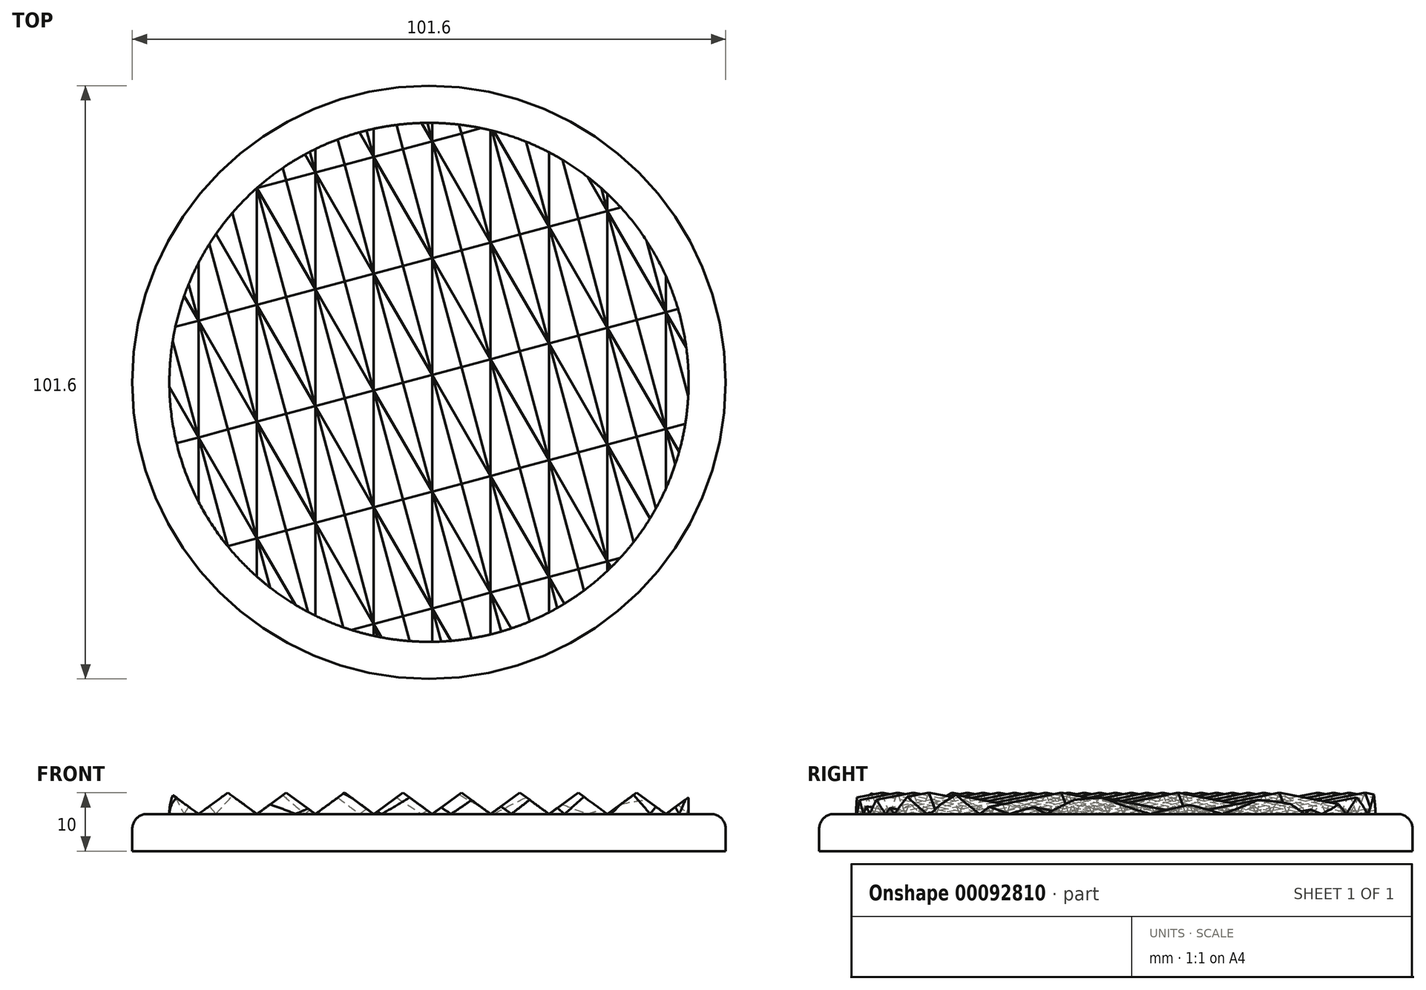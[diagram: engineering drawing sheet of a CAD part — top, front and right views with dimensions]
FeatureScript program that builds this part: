
annotation { "Feature Type Name" : "Feature", "Feature Type Description" : "" }
export const myFeature = defineFeature(function(context is Context, id is Id, definition is map)
    precondition{}
    {
        {
            var Q0;
            Q0=qCreatedBy(makeId("Top.planeOp"),FACE);
            var sketch = newSketch(context, id + "F0", { "sketchPlane" : qUnion([Q0])});
            skCircle(sketch, "E0", {"center": v(0, 0) * mm, "radius": 50.8 * mm});
            skCircle(sketch, "E1.0", {"center": v(0, 0) * mm, "radius": 44.45 * mm});
            skLineSegment(sketch, "E2", {"start": v(0, 110.46) * mm, "end": v(0, -125.45) * mm, "construction": true});
            skLineSegment(sketch, "E3", {"start": v(-101.34, -44.45) * mm, "end": v(105.07, -44.45) * mm, "construction": true});
            skLineSegment(sketch, "E4", {"start": v(129.04, 23.18) * mm, "end": v(-73.12, -93.54) * mm, "construction": true});
            skPoint(sketch, "E5", {"position": v(0, -44.45) * mm});
            skPoint(sketch, "E6", {"position": v(22.23, -38.5) * mm});
            skSolve(sketch);
        }
        {
            var Q0;
            Q0=makeQuery(id+"F0.imprint","IMPRINT",FACE,{"disambiguationData":[TD([[makeQuery(id+"F0.imprint","IMPRINT",EDGE,{"derivedFrom":sQuery(id+"F0.wireOp",EDGE,"E0")}),1.0]])]});
            extrude(context, id + "F1", {"entities" : qUnion([Q0]), "depth" : 6.35 * mm});
        }
        {
            var Q0;
            Q0=makeQuery(id+"F0.imprint","IMPRINT",FACE,{"disambiguationData":[TD([[makeQuery(id+"F0.imprint","IMPRINT",EDGE,{"derivedFrom":sQuery(id+"F0.wireOp",EDGE,"E1.0")}),1.0]])]});
            extrude(context, id + "F2", {"entities" : qUnion([Q0]), "operationType" : NewBodyOperationType.ADD, "depth" : 10 * mm});
        }
        {
            var Q0;
            Q0=makeQuery(id+"F2.opExtrude","CAP_FACE",FACE,{"disambiguationData":[OSD([sQuery(id+"F0.wireOp",EDGE,"E1.0")])],"isStart":false});
            var sketch = newSketch(context, id + "F3", { "sketchPlane" : qUnion([Q0])});
            skPoint(sketch, "E7.0", {"position": v(0, -44.45) * mm});
            skPoint(sketch, "E7.1", {"position": v(22.23, -38.5) * mm});
            skLineSegment(sketch, "E8.0", {"start": v(-101.34, -44.45) * mm, "end": v(105.07, -44.45) * mm, "construction": true});
            skLineSegment(sketch, "E8.1", {"start": v(129.04, 23.18) * mm, "end": v(-73.12, -93.54) * mm, "construction": true});
            skPoint(sketch, "E9", {"position": v(11.91, -44.45) * mm});
            skLineSegment(sketch, "E10", {"start": v(-34.53, 128.88) * mm, "end": v(21.6, -80.6) * mm, "construction": true});
            skSolve(sketch);
        }
        {
            var Q0;
            Q0=sQuery(id+"F3.wireOp",EDGE,"E8.1");
            var Q1;
            Q1=sQuery(id+"F0.wireOp",VERTEX,"E6");
            cPlane(context, id + "F4", {"entities" : qUnion([Q0, Q1]), "cplaneType" : CPlaneType.LINE_ANGLE, "offset" : 152.4 * mm, "angle" : 0 * degree, "width" : 152.4 * mm, "height" : 152.4 * mm});
        }
        {
            var Q0;
            Q0=sQuery(id+"F3.wireOp",EDGE,"E8.0");
            var Q1;
            Q1=sQuery(id+"F0.wireOp",VERTEX,"E5");
            cPlane(context, id + "F5", {"entities" : qUnion([Q0, Q1]), "cplaneType" : CPlaneType.LINE_ANGLE, "offset" : 152.4 * mm, "angle" : 0 * degree, "width" : 152.4 * mm, "height" : 152.4 * mm});
        }
        {
            var Q0;
            Q0=qCreatedBy(id+"F5.planeOp",FACE);
            var sketch = newSketch(context, id + "F6", { "sketchPlane" : qUnion([Q0])});
            skPoint(sketch, "E11.0", {"position": v(0, 0) * mm});
            skLineSegment(sketch, "E12", {"start": v(0, 24.1) * mm, "end": v(0, -15.53) * mm, "construction": true});
            skLineSegment(sketch, "E13.0", {"start": v(-44.45, 10) * mm, "end": v(44.45, 10) * mm, "construction": true});
            skLineSegment(sketch, "E14.0", {"start": v(-50.8, 6.35) * mm, "end": v(50.8, 6.35) * mm, "construction": true});
            skLineSegment(sketch, "E15", {"start": v(44.45, 10) * mm, "end": v(39.45, 6.35) * mm});
            skLineSegment(sketch, "E16", {"start": v(39.45, 6.35) * mm, "end": v(34.45, 10) * mm});
            skLineSegment(sketch, "E17", {"start": v(34.45, 10) * mm, "end": v(44.45, 10) * mm});
            skLineSegment(sketch, "E18.1.0.0", {"start": v(24.45, 10) * mm, "end": v(34.45, 10) * mm});
            skLineSegment(sketch, "E18.1.0.1", {"start": v(29.45, 6.35) * mm, "end": v(24.45, 10) * mm});
            skLineSegment(sketch, "E18.1.0.2", {"start": v(34.45, 10) * mm, "end": v(29.45, 6.35) * mm});
            skLineSegment(sketch, "E18.2.0.0", {"start": v(14.45, 10) * mm, "end": v(24.45, 10) * mm});
            skLineSegment(sketch, "E18.2.0.1", {"start": v(19.45, 6.35) * mm, "end": v(14.45, 10) * mm});
            skLineSegment(sketch, "E18.2.0.2", {"start": v(24.45, 10) * mm, "end": v(19.45, 6.35) * mm});
            skLineSegment(sketch, "E18.3.0.0", {"start": v(4.45, 10) * mm, "end": v(14.45, 10) * mm});
            skLineSegment(sketch, "E18.3.0.1", {"start": v(9.45, 6.35) * mm, "end": v(4.45, 10) * mm});
            skLineSegment(sketch, "E18.3.0.2", {"start": v(14.45, 10) * mm, "end": v(9.45, 6.35) * mm});
            skLineSegment(sketch, "E18.4.0.0", {"start": v(-5.55, 10) * mm, "end": v(4.45, 10) * mm});
            skLineSegment(sketch, "E18.4.0.1", {"start": v(-0.55, 6.35) * mm, "end": v(-5.55, 10) * mm});
            skLineSegment(sketch, "E18.4.0.2", {"start": v(4.45, 10) * mm, "end": v(-0.55, 6.35) * mm});
            skLineSegment(sketch, "E18.5.0.0", {"start": v(-15.55, 10) * mm, "end": v(-5.55, 10) * mm});
            skLineSegment(sketch, "E18.5.0.1", {"start": v(-10.55, 6.35) * mm, "end": v(-15.55, 10) * mm});
            skLineSegment(sketch, "E18.5.0.2", {"start": v(-5.55, 10) * mm, "end": v(-10.55, 6.35) * mm});
            skLineSegment(sketch, "E18.6.0.0", {"start": v(-25.55, 10) * mm, "end": v(-15.55, 10) * mm});
            skLineSegment(sketch, "E18.6.0.1", {"start": v(-20.55, 6.35) * mm, "end": v(-25.55, 10) * mm});
            skLineSegment(sketch, "E18.6.0.2", {"start": v(-15.55, 10) * mm, "end": v(-20.55, 6.35) * mm});
            skLineSegment(sketch, "E18.7.0.0", {"start": v(-35.55, 10) * mm, "end": v(-25.55, 10) * mm});
            skLineSegment(sketch, "E18.7.0.1", {"start": v(-30.55, 6.35) * mm, "end": v(-35.55, 10) * mm});
            skLineSegment(sketch, "E18.7.0.2", {"start": v(-25.55, 10) * mm, "end": v(-30.55, 6.35) * mm});
            skLineSegment(sketch, "E18.8.0.0", {"start": v(-45.55, 10) * mm, "end": v(-35.55, 10) * mm});
            skLineSegment(sketch, "E18.8.0.1", {"start": v(-40.55, 6.35) * mm, "end": v(-45.55, 10) * mm});
            skLineSegment(sketch, "E18.8.0.2", {"start": v(-35.55, 10) * mm, "end": v(-40.55, 6.35) * mm});
            skLineSegment(sketch, "E18.direction1", {"start": v(34.45, 10) * mm, "end": v(24.45, 10) * mm, "construction": true});
            skSolve(sketch);
        }
        {
            var Q0;
            Q0=makeQuery(id+"F6.imprint","IMPRINT",FACE,{"disambiguationData":[TD([[makeQuery(id+"F6.imprint","IMPRINT",EDGE,{"derivedFrom":sQuery(id+"F6.wireOp",EDGE,"E15")}),-1.0]])]});
            var Q1;
            Q1=makeQuery(id+"F6.imprint","IMPRINT",FACE,{"disambiguationData":[TD([[makeQuery(id+"F6.imprint","IMPRINT",EDGE,{"derivedFrom":sQuery(id+"F6.wireOp",EDGE,"E18.1.0.0")}),-1.0]])]});
            var Q2;
            Q2=makeQuery(id+"F6.imprint","IMPRINT",FACE,{"disambiguationData":[TD([[makeQuery(id+"F6.imprint","IMPRINT",EDGE,{"derivedFrom":sQuery(id+"F6.wireOp",EDGE,"E18.2.0.0")}),-1.0]])]});
            var Q3;
            Q3=makeQuery(id+"F6.imprint","IMPRINT",FACE,{"disambiguationData":[TD([[makeQuery(id+"F6.imprint","IMPRINT",EDGE,{"derivedFrom":sQuery(id+"F6.wireOp",EDGE,"E18.3.0.0")}),-1.0]])]});
            var Q4;
            Q4=makeQuery(id+"F6.imprint","IMPRINT",FACE,{"disambiguationData":[TD([[makeQuery(id+"F6.imprint","IMPRINT",EDGE,{"derivedFrom":sQuery(id+"F6.wireOp",EDGE,"E18.4.0.0")}),-1.0]])]});
            var Q5;
            Q5=makeQuery(id+"F6.imprint","IMPRINT",FACE,{"disambiguationData":[TD([[makeQuery(id+"F6.imprint","IMPRINT",EDGE,{"derivedFrom":sQuery(id+"F6.wireOp",EDGE,"E18.5.0.0")}),-1.0]])]});
            var Q6;
            Q6=makeQuery(id+"F6.imprint","IMPRINT",FACE,{"disambiguationData":[TD([[makeQuery(id+"F6.imprint","IMPRINT",EDGE,{"derivedFrom":sQuery(id+"F6.wireOp",EDGE,"E18.6.0.0")}),-1.0]])]});
            var Q7;
            Q7=makeQuery(id+"F6.imprint","IMPRINT",FACE,{"disambiguationData":[TD([[makeQuery(id+"F6.imprint","IMPRINT",EDGE,{"derivedFrom":sQuery(id+"F6.wireOp",EDGE,"E18.7.0.0")}),-1.0]])]});
            var Q8;
            Q8=makeQuery(id+"F6.imprint","IMPRINT",FACE,{"disambiguationData":[TD([[makeQuery(id+"F6.imprint","IMPRINT",EDGE,{"derivedFrom":sQuery(id+"F6.wireOp",EDGE,"E18.8.0.0")}),-1.0]])]});
            extrude(context, id + "F7", {"entities" : qUnion([Q0, Q1, Q2, Q3, Q4, Q5, Q6, Q7, Q8]), "operationType" : NewBodyOperationType.REMOVE, "depth" : 88.9 * mm});
        }
        {
            var Q0;
            Q0=qCreatedBy(id+"F4.planeOp",FACE);
            var sketch = newSketch(context, id + "F8", { "sketchPlane" : qUnion([Q0])});
            skPoint(sketch, "E19.0", {"position": v(0, 0) * mm});
            skLineSegment(sketch, "E20", {"start": v(0, 40.07) * mm, "end": v(0, -5.08) * mm, "construction": true});
            skLineSegment(sketch, "E21.0", {"start": v(-50.8, 6.35) * mm, "end": v(50.8, 6.35) * mm, "construction": true});
            skPoint(sketch, "E22.0", {"position": v(44.13, 10) * mm});
            skPoint(sketch, "E22.1", {"position": v(-43.88, 10) * mm});
            skLineSegment(sketch, "E23", {"start": v(-43.88, 10) * mm, "end": v(44.13, 10) * mm, "construction": true});
            skLineSegment(sketch, "E24", {"start": v(-43.88, 10) * mm, "end": v(-38.88, 6.35) * mm});
            skLineSegment(sketch, "E25", {"start": v(-38.88, 6.35) * mm, "end": v(-33.88, 10) * mm});
            skLineSegment(sketch, "E26", {"start": v(-33.88, 10) * mm, "end": v(-43.88, 10) * mm});
            skLineSegment(sketch, "E27.1.0.0", {"start": v(-28.88, 6.35) * mm, "end": v(-23.88, 10) * mm});
            skLineSegment(sketch, "E27.1.0.1", {"start": v(-23.88, 10) * mm, "end": v(-33.88, 10) * mm});
            skPoint(sketch, "E27.1.0.2", {"position": v(-33.88, 10) * mm});
            skLineSegment(sketch, "E27.1.0.3", {"start": v(-33.88, 10) * mm, "end": v(-28.88, 6.35) * mm});
            skLineSegment(sketch, "E27.2.0.0", {"start": v(-18.88, 6.35) * mm, "end": v(-13.88, 10) * mm});
            skLineSegment(sketch, "E27.2.0.1", {"start": v(-13.88, 10) * mm, "end": v(-23.88, 10) * mm});
            skPoint(sketch, "E27.2.0.2", {"position": v(-23.88, 10) * mm});
            skLineSegment(sketch, "E27.2.0.3", {"start": v(-23.88, 10) * mm, "end": v(-18.88, 6.35) * mm});
            skLineSegment(sketch, "E27.3.0.0", {"start": v(-8.88, 6.35) * mm, "end": v(-3.88, 10) * mm});
            skLineSegment(sketch, "E27.3.0.1", {"start": v(-3.88, 10) * mm, "end": v(-13.88, 10) * mm});
            skPoint(sketch, "E27.3.0.2", {"position": v(-13.88, 10) * mm});
            skLineSegment(sketch, "E27.3.0.3", {"start": v(-13.88, 10) * mm, "end": v(-8.88, 6.35) * mm});
            skLineSegment(sketch, "E27.4.0.0", {"start": v(1.12, 6.35) * mm, "end": v(6.12, 10) * mm});
            skLineSegment(sketch, "E27.4.0.1", {"start": v(6.12, 10) * mm, "end": v(-3.88, 10) * mm});
            skPoint(sketch, "E27.4.0.2", {"position": v(-3.88, 10) * mm});
            skLineSegment(sketch, "E27.4.0.3", {"start": v(-3.88, 10) * mm, "end": v(1.12, 6.35) * mm});
            skLineSegment(sketch, "E27.5.0.0", {"start": v(11.12, 6.35) * mm, "end": v(16.12, 10) * mm});
            skLineSegment(sketch, "E27.5.0.1", {"start": v(16.12, 10) * mm, "end": v(6.12, 10) * mm});
            skPoint(sketch, "E27.5.0.2", {"position": v(6.12, 10) * mm});
            skLineSegment(sketch, "E27.5.0.3", {"start": v(6.12, 10) * mm, "end": v(11.12, 6.35) * mm});
            skLineSegment(sketch, "E27.6.0.0", {"start": v(21.12, 6.35) * mm, "end": v(26.12, 10) * mm});
            skLineSegment(sketch, "E27.6.0.1", {"start": v(26.12, 10) * mm, "end": v(16.12, 10) * mm});
            skPoint(sketch, "E27.6.0.2", {"position": v(16.12, 10) * mm});
            skLineSegment(sketch, "E27.6.0.3", {"start": v(16.12, 10) * mm, "end": v(21.12, 6.35) * mm});
            skLineSegment(sketch, "E27.7.0.0", {"start": v(31.12, 6.35) * mm, "end": v(36.12, 10) * mm});
            skLineSegment(sketch, "E27.7.0.1", {"start": v(36.12, 10) * mm, "end": v(26.12, 10) * mm});
            skPoint(sketch, "E27.7.0.2", {"position": v(26.12, 10) * mm});
            skLineSegment(sketch, "E27.7.0.3", {"start": v(26.12, 10) * mm, "end": v(31.12, 6.35) * mm});
            skLineSegment(sketch, "E27.8.0.0", {"start": v(41.12, 6.35) * mm, "end": v(46.12, 10) * mm});
            skLineSegment(sketch, "E27.8.0.1", {"start": v(46.12, 10) * mm, "end": v(36.12, 10) * mm});
            skPoint(sketch, "E27.8.0.2", {"position": v(36.12, 10) * mm});
            skLineSegment(sketch, "E27.8.0.3", {"start": v(36.12, 10) * mm, "end": v(41.12, 6.35) * mm});
            skLineSegment(sketch, "E27.direction1", {"start": v(-38.88, 6.35) * mm, "end": v(-28.88, 6.35) * mm, "construction": true});
            skSolve(sketch);
        }
        {
            var Q0;
            Q0=makeQuery(id+"F8.imprint","IMPRINT",FACE,{"disambiguationData":[TD([[makeQuery(id+"F8.imprint","IMPRINT",EDGE,{"derivedFrom":sQuery(id+"F8.wireOp",EDGE,"E24")}),1.0]])]});
            var Q1;
            Q1=makeQuery(id+"F8.imprint","IMPRINT",FACE,{"disambiguationData":[TD([[makeQuery(id+"F8.imprint","IMPRINT",EDGE,{"derivedFrom":sQuery(id+"F8.wireOp",EDGE,"E27.1.0.0")}),1.0]])]});
            var Q2;
            Q2=makeQuery(id+"F8.imprint","IMPRINT",FACE,{"disambiguationData":[TD([[makeQuery(id+"F8.imprint","IMPRINT",EDGE,{"derivedFrom":sQuery(id+"F8.wireOp",EDGE,"E27.2.0.0")}),1.0]])]});
            var Q3;
            Q3=makeQuery(id+"F8.imprint","IMPRINT",FACE,{"disambiguationData":[TD([[makeQuery(id+"F8.imprint","IMPRINT",EDGE,{"derivedFrom":sQuery(id+"F8.wireOp",EDGE,"E27.3.0.0")}),1.0]])]});
            var Q4;
            Q4=makeQuery(id+"F8.imprint","IMPRINT",FACE,{"disambiguationData":[TD([[makeQuery(id+"F8.imprint","IMPRINT",EDGE,{"derivedFrom":sQuery(id+"F8.wireOp",EDGE,"E27.4.0.0")}),1.0]])]});
            var Q5;
            Q5=makeQuery(id+"F8.imprint","IMPRINT",FACE,{"disambiguationData":[TD([[makeQuery(id+"F8.imprint","IMPRINT",EDGE,{"derivedFrom":sQuery(id+"F8.wireOp",EDGE,"E27.5.0.0")}),1.0]])]});
            var Q6;
            Q6=makeQuery(id+"F8.imprint","IMPRINT",FACE,{"disambiguationData":[TD([[makeQuery(id+"F8.imprint","IMPRINT",EDGE,{"derivedFrom":sQuery(id+"F8.wireOp",EDGE,"E27.6.0.0")}),1.0]])]});
            var Q7;
            Q7=makeQuery(id+"F8.imprint","IMPRINT",FACE,{"disambiguationData":[TD([[makeQuery(id+"F8.imprint","IMPRINT",EDGE,{"derivedFrom":sQuery(id+"F8.wireOp",EDGE,"E27.7.0.0")}),1.0]])]});
            var Q8;
            Q8=makeQuery(id+"F8.imprint","IMPRINT",FACE,{"disambiguationData":[TD([[makeQuery(id+"F8.imprint","IMPRINT",EDGE,{"derivedFrom":sQuery(id+"F8.wireOp",EDGE,"E27.8.0.0")}),1.0]])]});
            extrude(context, id + "F9", {"entities" : qUnion([Q0, Q1, Q2, Q3, Q4, Q5, Q6, Q7, Q8]), "operationType" : NewBodyOperationType.REMOVE, "oppositeDirection" : true, "depth" : 88.9 * mm});
        }
        {
            var Q0;
            Q0=makeQuery(id+"F1.opExtrude","CAP_EDGE",EDGE,{"disambiguationData":[OSD([sQuery(id+"F0.wireOp",EDGE,"E0")])],"isStart":false});
            fillet(context, id + "F10", {"entities" : qUnion([Q0]), "radius" : 2.54 * mm, "tangentPropagation" : true, "allowEdgeOverflow" : false});
        }
    });
